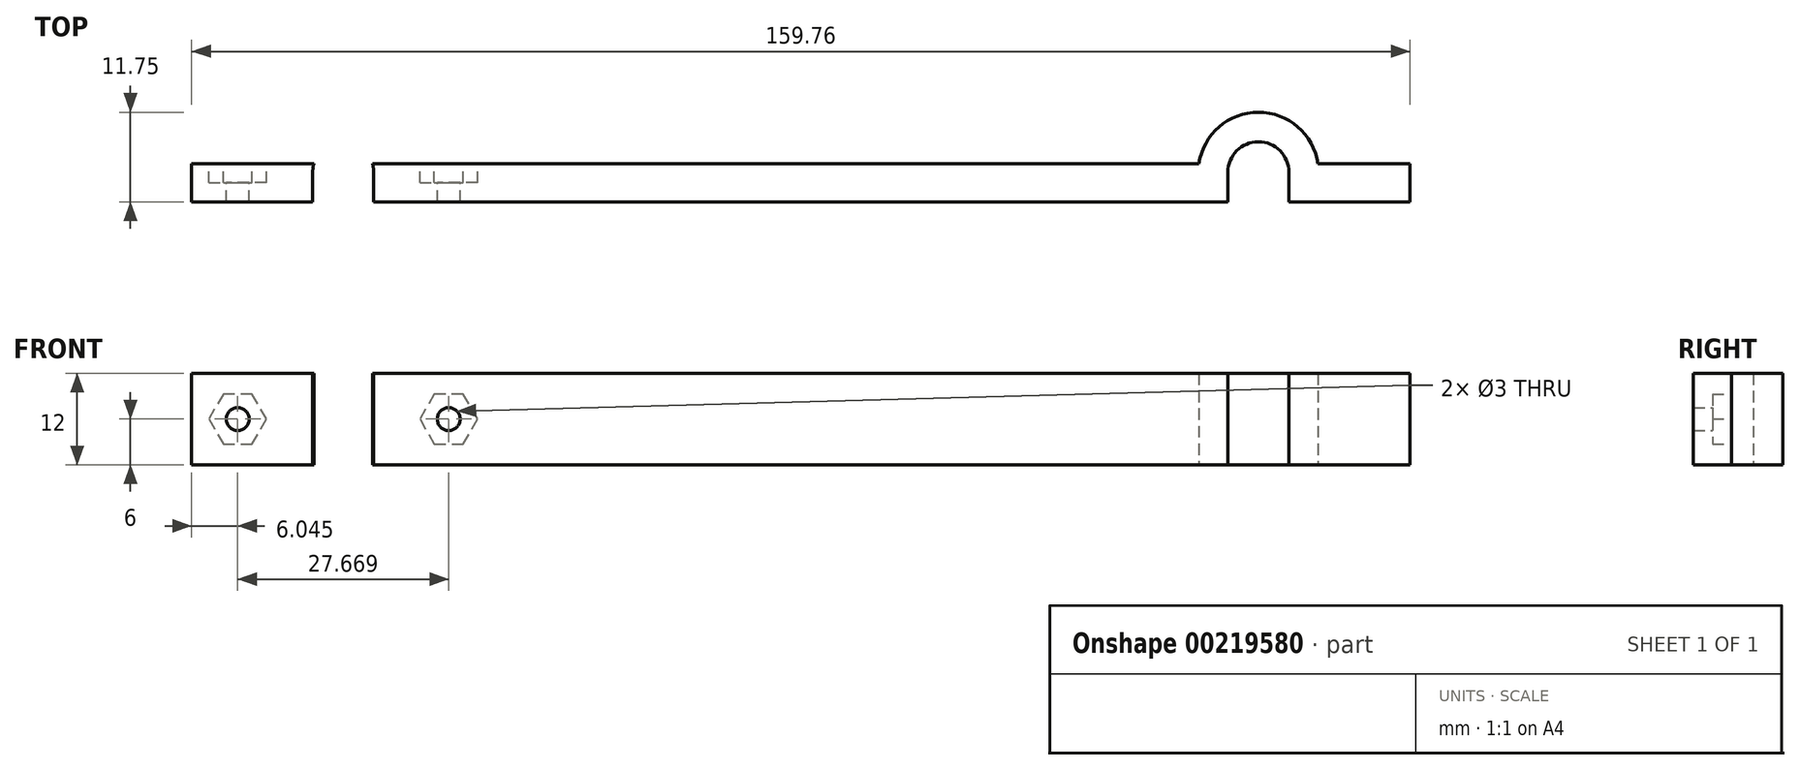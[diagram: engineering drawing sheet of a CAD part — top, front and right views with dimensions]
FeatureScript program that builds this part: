
annotation { "Feature Type Name" : "Feature", "Feature Type Description" : "" }
export const myFeature = defineFeature(function(context is Context, id is Id, definition is map)
    precondition{}
    {
        {
            var Q0;
            Q0=qCreatedBy(makeId("Top.planeOp"),FACE);
            var sketch = newSketch(context, id + "F0", { "sketchPlane" : qUnion([Q0])});
            skLineSegment(sketch, "E0.bottom", {"start": v(-79.88, 5) * mm, "end": v(79.88, 5) * mm});
            skLineSegment(sketch, "E0.top", {"start": v(-79.88, 0) * mm, "end": v(79.88, 0) * mm});
            skLineSegment(sketch, "E0.left", {"start": v(-79.88, 5) * mm, "end": v(-79.88, 0) * mm});
            skLineSegment(sketch, "E0.right", {"start": v(79.88, 5) * mm, "end": v(79.88, 0) * mm});
            skLineSegment(sketch, "E1.bottom", {"start": v(-67.88, 0) * mm, "end": v(-64, 0) * mm});
            skLineSegment(sketch, "E1.top", {"start": v(-67.88, 3.87) * mm, "end": v(-64, 3.87) * mm});
            skLineSegment(sketch, "E1.left", {"start": v(-67.88, 0) * mm, "end": v(-67.88, 3.87) * mm});
            skLineSegment(sketch, "E1.right", {"start": v(-64, 0) * mm, "end": v(-64, 3.88) * mm});
            skLineSegment(sketch, "E2.bottom", {"start": v(-56, 0) * mm, "end": v(-52.12, 0) * mm});
            skLineSegment(sketch, "E2.top", {"start": v(-56, 3.88) * mm, "end": v(-52.12, 3.88) * mm});
            skLineSegment(sketch, "E2.left", {"start": v(-56, 0) * mm, "end": v(-56, 3.88) * mm});
            skLineSegment(sketch, "E2.right", {"start": v(-52.12, 0) * mm, "end": v(-52.12, 3.88) * mm});
            skLineSegment(sketch, "E3.bottom", {"start": v(52.12, 3.88) * mm, "end": v(56, 3.88) * mm});
            skLineSegment(sketch, "E3.top", {"start": v(52.12, 0) * mm, "end": v(56, 0) * mm});
            skLineSegment(sketch, "E3.left", {"start": v(52.12, 3.88) * mm, "end": v(52.12, 0) * mm});
            skLineSegment(sketch, "E3.right", {"start": v(56, 3.87) * mm, "end": v(56, 0) * mm});
            skLineSegment(sketch, "E4.bottom", {"start": v(64, 3.88) * mm, "end": v(67.88, 3.88) * mm});
            skLineSegment(sketch, "E4.top", {"start": v(64, 0) * mm, "end": v(67.88, 0) * mm});
            skLineSegment(sketch, "E4.left", {"start": v(64, 3.88) * mm, "end": v(64, 0) * mm});
            skLineSegment(sketch, "E4.right", {"start": v(67.88, 3.88) * mm, "end": v(67.88, 0) * mm});
            skArc(sketch, "E5", {"start": v(-56, 3.88) * mm, "mid": v(-60, 7.88) * mm, "end": v(-64, 3.88) * mm});
            skArc(sketch, "E6", {"start": v(-52.12, 3.88) * mm, "mid": v(-60, 11.75) * mm, "end": v(-67.88, 3.87) * mm});
            skArc(sketch, "E7", {"start": v(64, 3.88) * mm, "mid": v(60, 7.88) * mm, "end": v(56, 3.87) * mm});
            skArc(sketch, "E8", {"start": v(67.88, 3.88) * mm, "mid": v(60, 11.75) * mm, "end": v(52.13, 3.88) * mm});
            skSolve(sketch);
        }
        {
            var Q0;
            {var subQ0=sQuery(id+"F0.wireOp",EDGE,"E0.left");Q0=makeQuery(id+"F0.imprint","IMPRINT",FACE,{"disambiguationData":[TD([[makeQuery(id+"F0.imprint","IMPRINT",EDGE,{"derivedFrom":subQ0}),1.0]])]});}
            var Q1;
            {var subQ0=sQuery(id+"F0.wireOp",EDGE,"E0.right");Q1=makeQuery(id+"F0.imprint","IMPRINT",FACE,{"disambiguationData":[TD([[makeQuery(id+"F0.imprint","IMPRINT",EDGE,{"derivedFrom":subQ0}),-1.0]])]});}
            var Q2;
            {var subQ0=sQuery(id+"F0.wireOp",EDGE,"E2.right");var subQ1=sQuery(id+"F0.wireOp",EDGE,"E0.bottom");var subQ2=makeQuery(id+"F0.imprint","INTERSECT",VERTEX,{"derivedFrom":[subQ1,subQ0]});Q2=makeQuery(id+"F0.imprint","IMPRINT",FACE,{"disambiguationData":[TD([[makeQuery(id+"F0.imprint","IMPRINT",EDGE,{"disambiguationData":[TD([[subQ2,-1.0]])],"derivedFrom":subQ1}),-1.0]])]});}
            var Q3;
            {var subQ5=sQuery(id+"F0.wireOp",EDGE,"E1.bottom");Q3=makeQuery(id+"F0.imprint","IMPRINT",FACE,{"disambiguationData":[TD([[makeQuery(id+"F0.imprint","IMPRINT",EDGE,{"derivedFrom":subQ5}),1.0]])]});}
            var Q4;
            {var subQ5=sQuery(id+"F0.wireOp",EDGE,"E1.top");Q4=makeQuery(id+"F0.imprint","IMPRINT",FACE,{"disambiguationData":[TD([[makeQuery(id+"F0.imprint","IMPRINT",EDGE,{"derivedFrom":subQ5}),-1.0]])]});}
            var Q5;
            {var subQ5=sQuery(id+"F0.wireOp",EDGE,"E2.bottom");Q5=makeQuery(id+"F0.imprint","IMPRINT",FACE,{"disambiguationData":[TD([[makeQuery(id+"F0.imprint","IMPRINT",EDGE,{"derivedFrom":subQ5}),1.0]])]});}
            var Q6;
            {var subQ5=sQuery(id+"F0.wireOp",EDGE,"E2.top");Q6=makeQuery(id+"F0.imprint","IMPRINT",FACE,{"disambiguationData":[TD([[makeQuery(id+"F0.imprint","IMPRINT",EDGE,{"derivedFrom":subQ5}),-1.0]])]});}
            var Q7;
            {var subQ5=sQuery(id+"F0.wireOp",EDGE,"E3.bottom");Q7=makeQuery(id+"F0.imprint","IMPRINT",FACE,{"disambiguationData":[TD([[makeQuery(id+"F0.imprint","IMPRINT",EDGE,{"derivedFrom":subQ5}),-1.0]])]});}
            var Q8;
            {var subQ5=sQuery(id+"F0.wireOp",EDGE,"E3.top");Q8=makeQuery(id+"F0.imprint","IMPRINT",FACE,{"disambiguationData":[TD([[makeQuery(id+"F0.imprint","IMPRINT",EDGE,{"derivedFrom":subQ5}),1.0]])]});}
            var Q9;
            {var subQ5=sQuery(id+"F0.wireOp",EDGE,"E4.bottom");Q9=makeQuery(id+"F0.imprint","IMPRINT",FACE,{"disambiguationData":[TD([[makeQuery(id+"F0.imprint","IMPRINT",EDGE,{"derivedFrom":subQ5}),-1.0]])]});}
            var Q10;
            {var subQ5=sQuery(id+"F0.wireOp",EDGE,"E4.top");Q10=makeQuery(id+"F0.imprint","IMPRINT",FACE,{"disambiguationData":[TD([[makeQuery(id+"F0.imprint","IMPRINT",EDGE,{"derivedFrom":subQ5}),1.0]])]});}
            var Q11;
            Q11=makeQuery(id+"F0.imprint","IMPRINT",FACE,{"disambiguationData":[TD([[makeQuery(id+"F0.imprint","IMPRINT",EDGE,{"derivedFrom":sQuery(id+"F0.wireOp",EDGE,"E1.top")}),1.0]])]});
            var Q12;
            Q12=makeQuery(id+"F0.imprint","IMPRINT",FACE,{"disambiguationData":[TD([[makeQuery(id+"F0.imprint","IMPRINT",EDGE,{"derivedFrom":sQuery(id+"F0.wireOp",EDGE,"E3.bottom")}),1.0]])]});
            var Q13;
            {var subQ0=sQuery(id+"F0.wireOp",EDGE,"E8");var subQ1=sQuery(id+"F0.wireOp",EDGE,"E0.bottom");var subQ2=makeQuery(id+"F0.imprint","INTERSECT",VERTEX,{"disambiguationData":[OD(0.0)],"derivedFrom":[subQ1,subQ0]});Q13=makeQuery(id+"F0.imprint","IMPRINT",FACE,{"disambiguationData":[TD([[makeQuery(id+"F0.imprint","IMPRINT",EDGE,{"disambiguationData":[TD([[subQ2,-1.0]])],"derivedFrom":subQ1}),1.0]])]});}
            var Q14;
            {var subQ0=sQuery(id+"F0.wireOp",EDGE,"E2.right");Q14=makeQuery(id+"F0.imprint","IMPRINT",FACE,{"disambiguationData":[TD([[makeQuery(id+"F0.imprint","IMPRINT",EDGE,{"derivedFrom":subQ0}),-1.0]])]});}
            var Q15;
            {var subQ0=sQuery(id+"F0.wireOp",EDGE,"E6");var subQ1=sQuery(id+"F0.wireOp",EDGE,"E0.bottom");var subQ2=makeQuery(id+"F0.imprint","INTERSECT",VERTEX,{"disambiguationData":[OD(0.0)],"derivedFrom":[subQ1,subQ0]});Q15=makeQuery(id+"F0.imprint","IMPRINT",FACE,{"disambiguationData":[TD([[makeQuery(id+"F0.imprint","IMPRINT",EDGE,{"disambiguationData":[TD([[subQ2,-1.0]])],"derivedFrom":subQ1}),1.0]])]});}
            extrude(context, id + "F1", {"entities" : qUnion([Q0, Q1, Q2, Q3, Q4, Q5, Q6, Q7, Q8, Q9, Q10, Q11, Q12, Q13, Q14, Q15]), "depth" : 12 * mm});
        }
        {
            var Q0;
            {var subQ0=sQuery(id+"F0.wireOp",EDGE,"E0.bottom");Q0=makeQuery(id+"F1.opExtrude","SWEPT_FACE",FACE,{"disambiguationData":[OSD([subQ0]),TDD([makeQuery(id+"F0.imprint","IMPRINT",EDGE,{"disambiguationData":[TD([[makeQuery(id+"F0.imprint","INTERSECT",VERTEX,{"derivedFrom":[subQ0,sQuery(id+"F0.wireOp",EDGE,"E2.right")]}),-1.0]])],"derivedFrom":subQ0})])]});}
            var sketch = newSketch(context, id + "F2", { "sketchPlane" : qUnion([Q0])});
            skCircle(sketch, "E9.cCircle", {"center": v(46.17, 6) * mm, "radius": 3.28 * mm, "construction": true});
            skPoint(sketch, "E9.cCircle.centerSnap0", {"position": v(79.88, 6) * mm});
            skLineSegment(sketch, "E9.0", {"start": v(48.06, 2.73) * mm, "end": v(44.27, 2.73) * mm});
            skLineSegment(sketch, "E9.1", {"start": v(44.27, 2.72) * mm, "end": v(42.38, 6) * mm});
            skLineSegment(sketch, "E9.2", {"start": v(42.38, 6) * mm, "end": v(44.27, 9.28) * mm});
            skLineSegment(sketch, "E9.3", {"start": v(44.27, 9.28) * mm, "end": v(48.06, 9.28) * mm});
            skLineSegment(sketch, "E9.4", {"start": v(48.06, 9.28) * mm, "end": v(49.95, 6) * mm});
            skLineSegment(sketch, "E9.5", {"start": v(49.95, 6) * mm, "end": v(48.06, 2.72) * mm});
            skPoint(sketch, "E9.0.midPoint", {"position": v(46.17, 2.73) * mm});
            skCircle(sketch, "E10.cCircle", {"center": v(73.83, 6) * mm, "radius": 3.28 * mm, "construction": true});
            skLineSegment(sketch, "E10.0", {"start": v(75.73, 2.73) * mm, "end": v(71.94, 2.73) * mm});
            skLineSegment(sketch, "E10.1", {"start": v(71.94, 2.73) * mm, "end": v(70.05, 6) * mm});
            skLineSegment(sketch, "E10.2", {"start": v(70.05, 6) * mm, "end": v(71.94, 9.27) * mm});
            skLineSegment(sketch, "E10.3", {"start": v(71.94, 9.27) * mm, "end": v(75.73, 9.27) * mm});
            skLineSegment(sketch, "E10.4", {"start": v(75.73, 9.27) * mm, "end": v(77.62, 6) * mm});
            skLineSegment(sketch, "E10.5", {"start": v(77.62, 6) * mm, "end": v(75.73, 2.73) * mm});
            skPoint(sketch, "E10.0.midPoint", {"position": v(73.83, 2.73) * mm});
            skLineSegment(sketch, "E11", {"start": v(46.17, 6) * mm, "end": v(0, 6) * mm, "construction": true});
            skLineSegment(sketch, "E12", {"start": v(46.17, 6) * mm, "end": v(73.83, 6) * mm, "construction": true});
            skLineSegment(sketch, "E13", {"start": v(60, 6) * mm, "end": v(60, 0) * mm, "construction": true});
            skSolve(sketch);
        }
        {
            var Q0;
            Q0 = qSketchRegion(id + "F2", true);
            extrude(context, id + "F3", {"entities" : qUnion([Q0]), "operationType" : NewBodyOperationType.REMOVE, "oppositeDirection" : true, "depth" : 2.5 * mm});
        }
        {
            var Q0;
            {var subQ0=sQuery(id+"F0.wireOp",EDGE,"E0.bottom");Q0=makeQuery(id+"F1.opExtrude","SWEPT_FACE",FACE,{"disambiguationData":[OSD([subQ0]),TDD([makeQuery(id+"F0.imprint","IMPRINT",EDGE,{"disambiguationData":[TD([[makeQuery(id+"F0.imprint","INTERSECT",VERTEX,{"derivedFrom":[subQ0,sQuery(id+"F0.wireOp",EDGE,"E2.right")]}),-1.0]])],"derivedFrom":subQ0})])]});}
            var sketch = newSketch(context, id + "F4", { "sketchPlane" : qUnion([Q0])});
            skCircle(sketch, "E14", {"center": v(46.17, 6) * mm, "radius": 1.5 * mm});
            skPoint(sketch, "E14.centerSnap0", {"position": v(46.17, 2.73) * mm});
            skCircle(sketch, "E15", {"center": v(73.83, 6) * mm, "radius": 1.5 * mm});
            skSolve(sketch);
        }
        {
            var Q0;
            Q0 = qSketchRegion(id + "F4", true);
            extrude(context, id + "F5", {"entities" : qUnion([Q0]), "operationType" : NewBodyOperationType.REMOVE, "endBound" : BoundingType.THROUGH_ALL, "oppositeDirection" : true, "depth" : 25 * mm});
        }
    });
